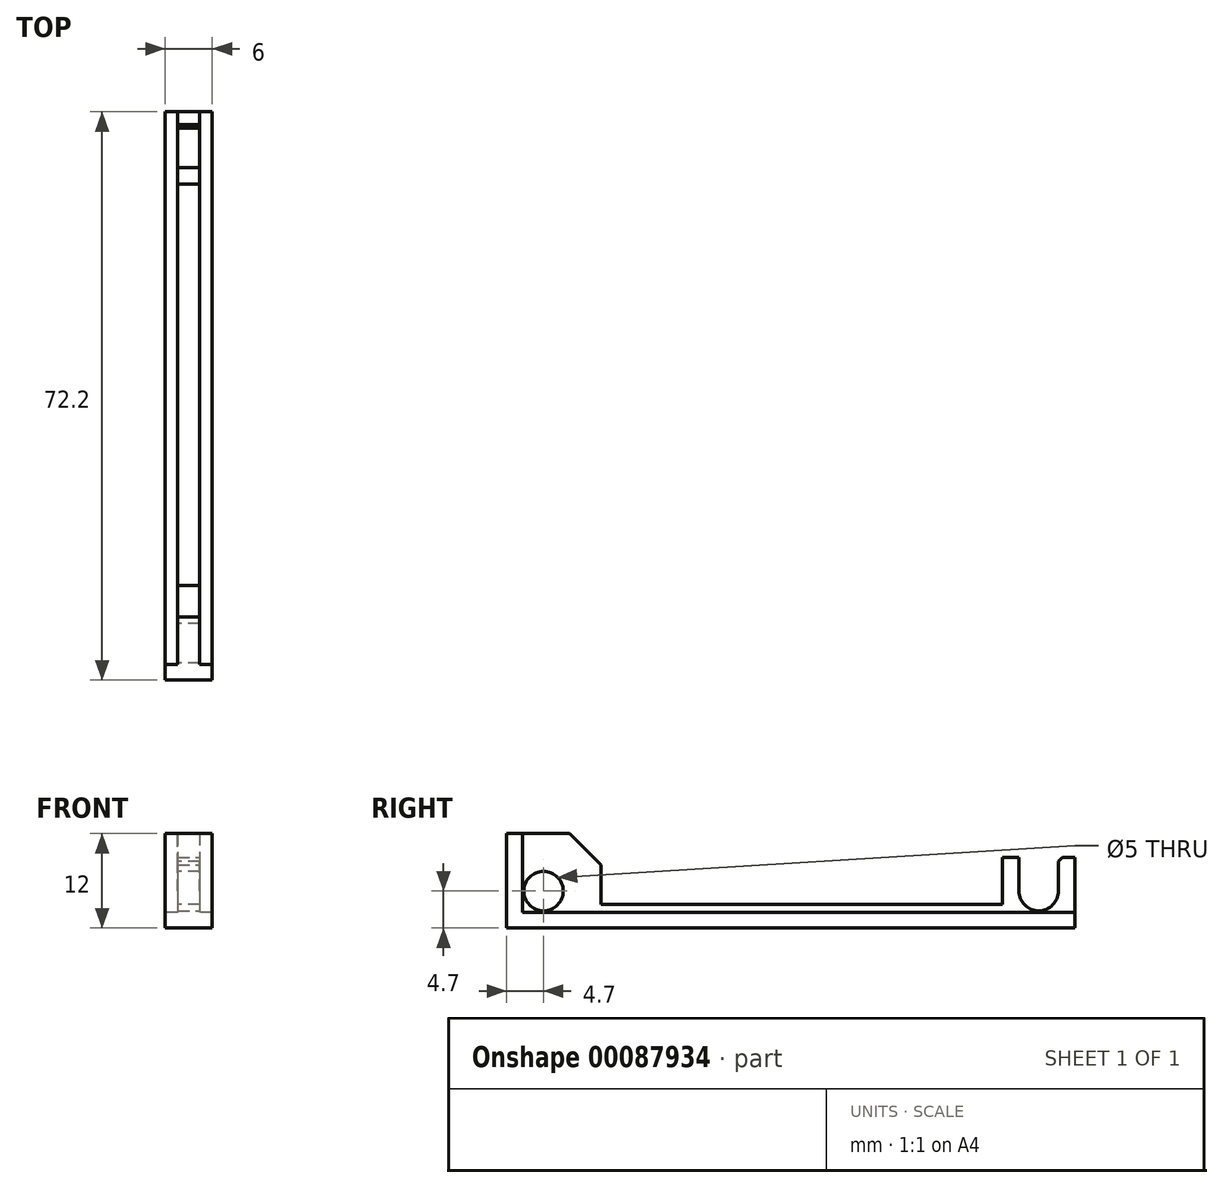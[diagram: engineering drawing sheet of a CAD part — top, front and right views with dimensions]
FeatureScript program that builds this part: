
annotation { "Feature Type Name" : "Feature", "Feature Type Description" : "" }
export const myFeature = defineFeature(function(context is Context, id is Id, definition is map)
    precondition{}
    {
        {
            var Q0;
            Q0=qCreatedBy(makeId("Top.planeOp"),FACE);
            var sketch = newSketch(context, id + "F0", { "sketchPlane" : qUnion([Q0])});
            skLineSegment(sketch, "E0.bottom", {"start": v(0, 0) * mm, "end": v(6, 0) * mm});
            skLineSegment(sketch, "E0.top", {"start": v(0, -10) * mm, "end": v(6, -10) * mm});
            skLineSegment(sketch, "E0.left", {"start": v(0, 0) * mm, "end": v(0, -10) * mm});
            skLineSegment(sketch, "E0.right", {"start": v(6, 0) * mm, "end": v(6, -10) * mm});
            skSolve(sketch);
        }
        {
            var Q0;
            Q0=makeQuery(id+"F0.imprint","IMPRINT",FACE,{"disambiguationData":[TD([[makeQuery(id+"F0.imprint","IMPRINT",EDGE,{"derivedFrom":sQuery(id+"F0.wireOp",EDGE,"E0.bottom")}),-1.0]])]});
            extrude(context, id + "F1", {"entities" : qUnion([Q0]), "depth" : 2 * mm});
        }
        {
            var Q0;
            Q0=makeQuery(id+"F1.opExtrude","CAP_FACE",FACE,{"disambiguationData":[OSD([sQuery(id+"F0.wireOp",EDGE,"E0.bottom"),sQuery(id+"F0.wireOp",EDGE,"E0.top"),sQuery(id+"F0.wireOp",EDGE,"E0.left"),sQuery(id+"F0.wireOp",EDGE,"E0.right")])],"isStart":false});
            var sketch = newSketch(context, id + "F2", { "sketchPlane" : qUnion([Q0])});
            skLineSegment(sketch, "E1.bottom", {"start": v(1.6, 0) * mm, "end": v(4.4, 0) * mm});
            skLineSegment(sketch, "E1.top", {"start": v(1.6, -10) * mm, "end": v(4.4, -10) * mm});
            skLineSegment(sketch, "E1.left", {"start": v(1.6, 0) * mm, "end": v(1.6, -10) * mm});
            skLineSegment(sketch, "E1.right", {"start": v(4.4, 0) * mm, "end": v(4.4, -10) * mm});
            skSolve(sketch);
        }
        {
            var Q0;
            Q0=makeQuery(id+"F2.imprint","IMPRINT",FACE,{"disambiguationData":[TD([[makeQuery(id+"F2.imprint","IMPRINT",EDGE,{"derivedFrom":sQuery(id+"F2.wireOp",EDGE,"E1.bottom")}),-1.0]])]});
            extrude(context, id + "F3", {"entities" : qUnion([Q0]), "operationType" : NewBodyOperationType.ADD, "depth" : 10 * mm});
        }
        {
            var Q0;
            Q0=makeQuery(id+"F3.opExtrude","CAP_FACE",FACE,{"disambiguationData":[OSD([sQuery(id+"F2.wireOp",EDGE,"E1.bottom"),sQuery(id+"F2.wireOp",EDGE,"E1.top"),sQuery(id+"F2.wireOp",EDGE,"E1.left"),sQuery(id+"F2.wireOp",EDGE,"E1.right")])],"isStart":false});
            extrude(context, id + "F4", {"entities" : qUnion([Q0]), "operationType" : NewBodyOperationType.REMOVE, "oppositeDirection" : true, "depth" : 3 * mm});
        }
        {
            var Q0;
            Q0=makeQuery(id+"F3.boolean.opBoolean","MERGE",FACE,{"derivedFrom":[makeQuery(id+"F1.opExtrude","SWEPT_FACE",FACE,{"disambiguationData":[OSD([sQuery(id+"F0.wireOp",EDGE,"E0.bottom")])]}),makeQuery(id+"F3.opExtrude","SWEPT_FACE",FACE,{"disambiguationData":[OSD([sQuery(id+"F2.wireOp",EDGE,"E1.bottom")])]})]});
            extrude(context, id + "F5", {"entities" : qUnion([Q0]), "operationType" : NewBodyOperationType.REMOVE, "oppositeDirection" : true, "depth" : .8 * mm});
        }
        {
            var Q0;
            Q0=makeQuery(id+"F3.opExtrude","SWEPT_FACE",FACE,{"disambiguationData":[OSD([sQuery(id+"F2.wireOp",EDGE,"E1.right")])]});
            var sketch = newSketch(context, id + "F6", { "sketchPlane" : qUnion([Q0])});
            skArc(sketch, "E2", {"start": v(-7.9, 4.7) * mm, "mid": v(-5.4, 2.2) * mm, "end": v(-2.9, 4.7) * mm});
            skPoint(sketch, "E2.centerSnap0", {"position": v(-5.4, 5.5) * mm});
            skPoint(sketch, "E3.trimOffspring.end.orphan", {"position": v(-10, 2) * mm});
            skPoint(sketch, "E4.start.orphan", {"position": v(-0.8, 9) * mm});
            skLineSegment(sketch, "E5.bottom", {"start": v(-2.9, 4.7) * mm, "end": v(-2.9, 4.7) * mm});
            skLineSegment(sketch, "E5.top", {"start": v(-7.9, 9) * mm, "end": v(-2.9, 9) * mm});
            skLineSegment(sketch, "E5.left", {"start": v(-7.9, 4.7) * mm, "end": v(-7.9, 9) * mm});
            skLineSegment(sketch, "E5.right", {"start": v(-2.9, 4.7) * mm, "end": v(-2.9, 9) * mm});
            skSolve(sketch);
        }
        {
            var Q0;
            Q0=makeQuery(id+"F6.imprint","IMPRINT",FACE,{"disambiguationData":[TD([[makeQuery(id+"F6.imprint","IMPRINT",EDGE,{"derivedFrom":sQuery(id+"F6.wireOp",EDGE,"E2")}),1.0]])]});
            extrude(context, id + "F7", {"entities" : qUnion([Q0]), "operationType" : NewBodyOperationType.REMOVE, "oppositeDirection" : true, "depth" : 25 * mm});
        }
        {
            var Q0;
            Q0=makeQuery(id+"F7.boolean.opBoolean","COPY",EDGE,{"derivedFrom":makeQuery(id+"F7.opExtrude","SWEPT_EDGE",EDGE,{"disambiguationData":[OSD([sQuery(id+"F2.wireOp",EDGE,"E1.right"),sQuery(id+"F6.wireOp",EDGE,"E5.top"),sQuery(id+"F6.wireOp",EDGE,"E5.left")])]})});
            var Q1;
            Q1=makeQuery(id+"F7.boolean.opBoolean","COPY",EDGE,{"derivedFrom":makeQuery(id+"F7.opExtrude","SWEPT_EDGE",EDGE,{"disambiguationData":[OSD([sQuery(id+"F2.wireOp",EDGE,"E1.right"),sQuery(id+"F6.wireOp",EDGE,"E5.top"),sQuery(id+"F6.wireOp",EDGE,"E5.right")])]})});
            var Q2;
            Q2=makeQuery(id+"F4.boolean.opBoolean","COPY",EDGE,{"derivedFrom":makeQuery(id+"F4.opExtrude","CAP_EDGE",EDGE,{"disambiguationData":[OSD([sQuery(id+"F2.wireOp",EDGE,"E1.top")])],"isStart":false})});
            var Q3;
            Q3=makeQuery(id+"F5.boolean.opBoolean","COPY",EDGE,{"derivedFrom":makeQuery(id+"F5.opExtrude","CAP_EDGE",EDGE,{"disambiguationData":[OSD([sQuery(id+"F2.wireOp",EDGE,"E1.bottom")])],"isStart":false})});
            chamfer(context, id + "F8", {"entities" : qUnion([Q0, Q1, Q2, Q3]), "width" : .5 * mm, "tangentPropagation" : true});
        }
        {
            var Q0;
            Q0=makeQuery(id+"F3.boolean.opBoolean","MERGE",FACE,{"derivedFrom":[makeQuery(id+"F1.opExtrude","SWEPT_FACE",FACE,{"disambiguationData":[OSD([sQuery(id+"F0.wireOp",EDGE,"E0.top")])]}),makeQuery(id+"F3.opExtrude","SWEPT_FACE",FACE,{"disambiguationData":[OSD([sQuery(id+"F2.wireOp",EDGE,"E1.top")])]})]});
            var sketch = newSketch(context, id + "F9", { "sketchPlane" : qUnion([Q0])});
            skLineSegment(sketch, "E6.bottom", {"start": v(0, 2) * mm, "end": v(6, 2) * mm});
            skLineSegment(sketch, "E6.top", {"start": v(0, 0) * mm, "end": v(6, 0) * mm});
            skLineSegment(sketch, "E6.left", {"start": v(0, 2) * mm, "end": v(0, 0) * mm});
            skLineSegment(sketch, "E6.right", {"start": v(6, 2) * mm, "end": v(6, 0) * mm});
            skSolve(sketch);
        }
        {
            var Q0;
            Q0=makeQuery(id+"F9.imprint","IMPRINT",FACE,{"disambiguationData":[TD([[makeQuery(id+"F9.imprint","IMPRINT",EDGE,{"derivedFrom":sQuery(id+"F9.wireOp",EDGE,"E6.top")}),1.0]])]});
            extrude(context, id + "F10", {"entities" : qUnion([Q0]), "operationType" : NewBodyOperationType.ADD, "depth" : 63 * mm});
        }
        {
            var Q0;
            {var subQ0=sQuery(id+"F0.wireOp",EDGE,"E0.right");var subQ2=sQuery(id+"F0.wireOp",EDGE,"E0.top");var subQ4=sQuery(id+"F0.wireOp",EDGE,"E0.bottom");var subQ7=sQuery(id+"F0.wireOp",EDGE,"E0.left");var subQ8=makeQuery(id+"F1.opExtrude","CAP_FACE",FACE,{"disambiguationData":[OSD([subQ4,subQ2,subQ7,subQ0])],"isStart":false});Q0=makeQuery(id+"F10.boolean.opBoolean","MERGE",FACE,{"derivedFrom":[makeQuery(id+"F3.boolean.opBoolean","SPLIT",FACE,{"disambiguationData":[TD([makeQuery(id+"F1.opExtrude","SWEPT_FACE",FACE,{"disambiguationData":[OSD([subQ7])]})])],"derivedFrom":subQ8}),makeQuery(id+"F3.boolean.opBoolean","SPLIT",FACE,{"disambiguationData":[TD([makeQuery(id+"F1.opExtrude","SWEPT_FACE",FACE,{"disambiguationData":[OSD([subQ0])]})])],"derivedFrom":subQ8}),makeQuery(id+"F10.opExtrude","SWEPT_FACE",FACE,{"disambiguationData":[OSD([sQuery(id+"F9.wireOp",EDGE,"E6.bottom")])]})]});}
            var sketch = newSketch(context, id + "F11", { "sketchPlane" : qUnion([Q0])});
            skLineSegment(sketch, "E7.bottom", {"start": v(6, -73) * mm, "end": v(0, -73) * mm});
            skLineSegment(sketch, "E7.top", {"start": v(6, -71) * mm, "end": v(0, -71) * mm});
            skLineSegment(sketch, "E7.left", {"start": v(6, -73) * mm, "end": v(6, -71) * mm});
            skLineSegment(sketch, "E7.right", {"start": v(0, -73) * mm, "end": v(0, -71) * mm});
            skSolve(sketch);
        }
        {
            var Q0;
            Q0=makeQuery(id+"F11.imprint","IMPRINT",FACE,{"disambiguationData":[TD([[makeQuery(id+"F11.imprint","IMPRINT",EDGE,{"derivedFrom":sQuery(id+"F11.wireOp",EDGE,"E7.bottom")}),1.0]])]});
            extrude(context, id + "F12", {"entities" : qUnion([Q0]), "operationType" : NewBodyOperationType.ADD, "depth" : 10 * mm});
        }
        {
            var Q0;
            Q0=makeQuery(id+"F12.opExtrude","SWEPT_FACE",FACE,{"disambiguationData":[OSD([sQuery(id+"F11.wireOp",EDGE,"E7.top")])]});
            var sketch = newSketch(context, id + "F13", { "sketchPlane" : qUnion([Q0])});
            skLineSegment(sketch, "E8.bottom", {"start": v(-4.4, 12) * mm, "end": v(-1.6, 12) * mm});
            skLineSegment(sketch, "E8.top", {"start": v(-4.4, 2) * mm, "end": v(-1.6, 2) * mm});
            skLineSegment(sketch, "E8.left", {"start": v(-4.4, 12) * mm, "end": v(-4.4, 2) * mm});
            skLineSegment(sketch, "E8.right", {"start": v(-1.6, 12) * mm, "end": v(-1.6, 2) * mm});
            skSolve(sketch);
        }
        {
            var Q0;
            Q0=makeQuery(id+"F13.imprint","IMPRINT",FACE,{"disambiguationData":[TD([[makeQuery(id+"F13.imprint","IMPRINT",EDGE,{"derivedFrom":sQuery(id+"F13.wireOp",EDGE,"E8.bottom")}),-1.0]])]});
            extrude(context, id + "F14", {"entities" : qUnion([Q0]), "operationType" : NewBodyOperationType.ADD, "depth" : 10 * mm});
        }
        {
            var Q0;
            Q0=makeQuery(id+"F14.opExtrude","SWEPT_FACE",FACE,{"disambiguationData":[OSD([sQuery(id+"F13.wireOp",EDGE,"E8.right")])]});
            var sketch = newSketch(context, id + "F15", { "sketchPlane" : qUnion([Q0])});
            skCircle(sketch, "E9", {"center": v(68.3, 4.7) * mm, "radius": 2.5 * mm});
            skSolve(sketch);
        }
        {
            var Q0;
            Q0=makeQuery(id+"F15.imprint","IMPRINT",FACE,{"disambiguationData":[TD([[makeQuery(id+"F15.imprint","IMPRINT",EDGE,{"derivedFrom":sQuery(id+"F15.wireOp",EDGE,"E9")}),1.0]])]});
            extrude(context, id + "F16", {"entities" : qUnion([Q0]), "operationType" : NewBodyOperationType.REMOVE, "oppositeDirection" : true, "depth" : 25 * mm});
        }
        {
            var Q0;
            Q0=makeQuery(id+"F14.opExtrude","CAP_EDGE",EDGE,{"disambiguationData":[OSD([sQuery(id+"F13.wireOp",EDGE,"E8.bottom")])],"isStart":false});
            chamfer(context, id + "F17", {"entities" : qUnion([Q0]), "width" : 4 * mm, "tangentPropagation" : true});
        }
        {
            var Q0;
            {var subQ0=sQuery(id+"F0.wireOp",EDGE,"E0.right");var subQ2=sQuery(id+"F0.wireOp",EDGE,"E0.top");var subQ4=sQuery(id+"F0.wireOp",EDGE,"E0.bottom");var subQ7=sQuery(id+"F0.wireOp",EDGE,"E0.left");var subQ8=makeQuery(id+"F1.opExtrude","CAP_FACE",FACE,{"disambiguationData":[OSD([subQ4,subQ2,subQ7,subQ0])],"isStart":false});Q0=makeQuery(id+"F10.boolean.opBoolean","MERGE",FACE,{"derivedFrom":[makeQuery(id+"F3.boolean.opBoolean","SPLIT",FACE,{"disambiguationData":[TD([makeQuery(id+"F1.opExtrude","SWEPT_FACE",FACE,{"disambiguationData":[OSD([subQ7])]})])],"derivedFrom":subQ8}),makeQuery(id+"F3.boolean.opBoolean","SPLIT",FACE,{"disambiguationData":[TD([makeQuery(id+"F1.opExtrude","SWEPT_FACE",FACE,{"disambiguationData":[OSD([subQ0])]})])],"derivedFrom":subQ8}),makeQuery(id+"F10.opExtrude","SWEPT_FACE",FACE,{"disambiguationData":[OSD([sQuery(id+"F9.wireOp",EDGE,"E6.bottom")])]})]});}
            var sketch = newSketch(context, id + "F18", { "sketchPlane" : qUnion([Q0])});
            skLineSegment(sketch, "E10.bottom", {"start": v(1.6, -61) * mm, "end": v(4.4, -61) * mm});
            skLineSegment(sketch, "E10.top", {"start": v(1.6, -10) * mm, "end": v(4.4, -10) * mm});
            skLineSegment(sketch, "E10.left", {"start": v(1.6, -61) * mm, "end": v(1.6, -10) * mm});
            skLineSegment(sketch, "E10.right", {"start": v(4.4, -61) * mm, "end": v(4.4, -10) * mm});
            skSolve(sketch);
        }
        {
            var Q0;
            Q0=makeQuery(id+"F18.imprint","IMPRINT",FACE,{"disambiguationData":[TD([[makeQuery(id+"F18.imprint","IMPRINT",EDGE,{"derivedFrom":sQuery(id+"F18.wireOp",EDGE,"E10.bottom")}),-1.0]])]});
            extrude(context, id + "F19", {"entities" : qUnion([Q0]), "operationType" : NewBodyOperationType.ADD, "depth" : 1 * mm});
        }
    });
